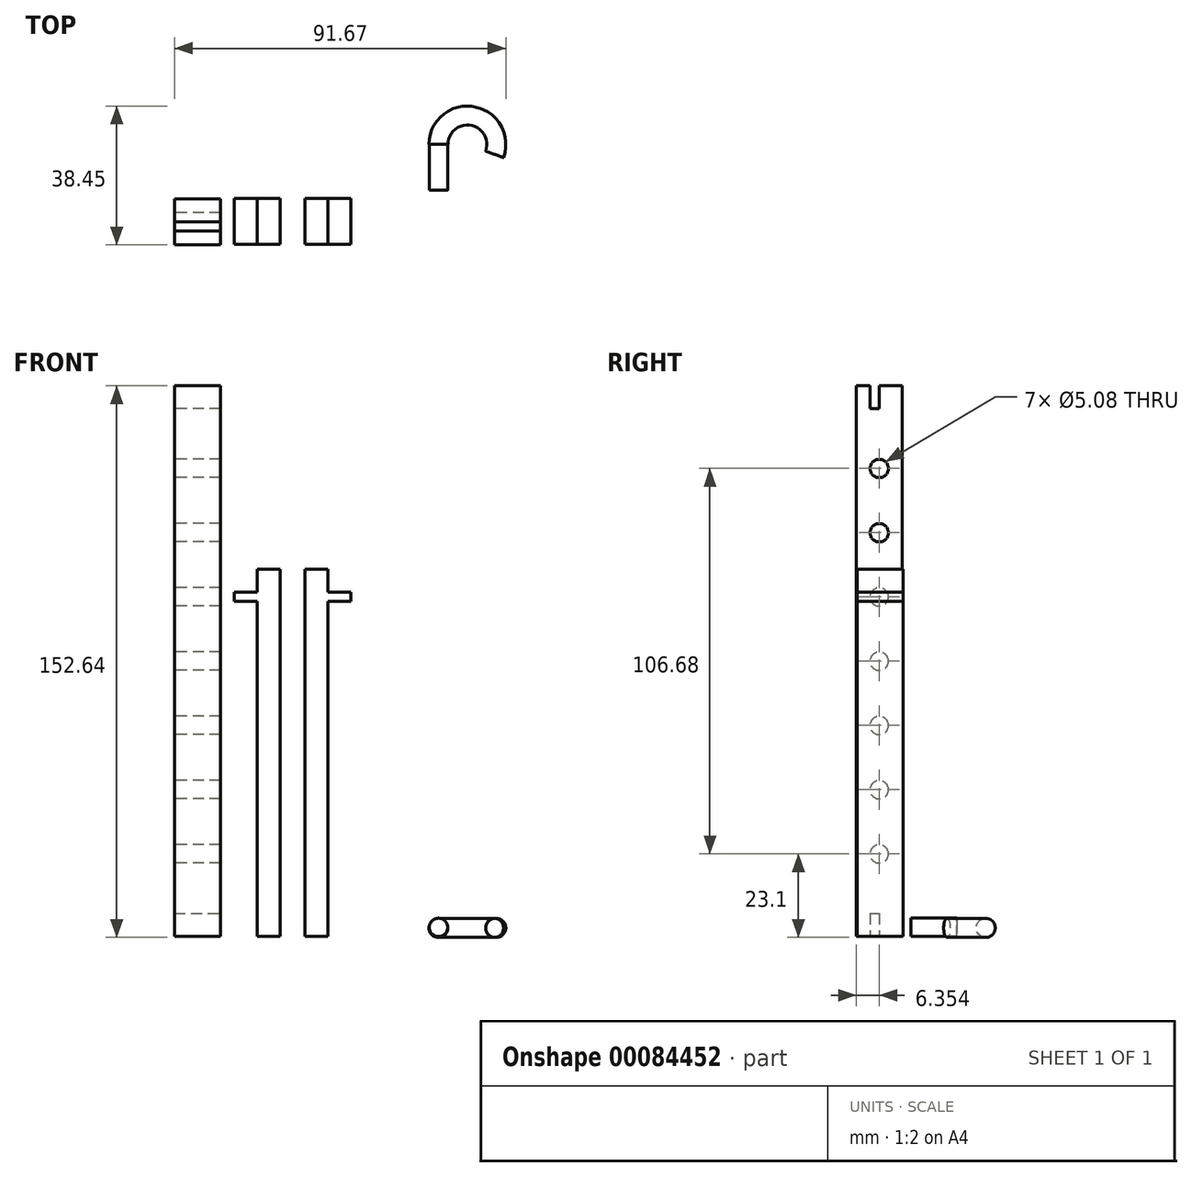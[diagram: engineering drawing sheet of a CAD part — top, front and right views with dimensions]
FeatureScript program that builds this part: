
annotation { "Feature Type Name" : "Feature", "Feature Type Description" : "" }
export const myFeature = defineFeature(function(context is Context, id is Id, definition is map)
    precondition{}
    {
        {
            var Q0;
            Q0=qCreatedBy(makeId("Top.planeOp"),FACE);
            var sketch = newSketch(context, id + "F0", { "sketchPlane" : qUnion([Q0])});
            skLineSegment(sketch, "E0.bottom", {"start": v(-10.38, -28.84) * mm, "end": v(-4.03, -28.84) * mm});
            skLineSegment(sketch, "E0.top", {"start": v(-10.38, -41.54) * mm, "end": v(-4.03, -41.54) * mm});
            skLineSegment(sketch, "E0.left", {"start": v(-10.38, -28.84) * mm, "end": v(-10.38, -41.54) * mm});
            skLineSegment(sketch, "E0.right", {"start": v(-4.03, -28.84) * mm, "end": v(-4.03, -41.54) * mm});
            skLineSegment(sketch, "E1.bottom", {"start": v(2.83, -28.77) * mm, "end": v(9.18, -28.77) * mm});
            skLineSegment(sketch, "E1.top", {"start": v(2.83, -41.47) * mm, "end": v(9.18, -41.47) * mm});
            skLineSegment(sketch, "E1.left", {"start": v(2.83, -28.77) * mm, "end": v(2.83, -41.47) * mm});
            skLineSegment(sketch, "E1.right", {"start": v(9.18, -28.77) * mm, "end": v(9.18, -41.47) * mm});
            skSolve(sketch);
        }
        {
            var Q0;
            Q0 = qSketchRegion(id + "F0", true);
            extrude(context, id + "F1", {"entities" : qUnion([Q0]), "depth" : 101.6 * mm});
        }
        {
            var Q0;
            Q0=makeQuery(id+"F1.opExtrude","SWEPT_FACE",FACE,{"disambiguationData":[OSD([sQuery(id+"F0.wireOp",EDGE,"E1.right")])]});
            var sketch = newSketch(context, id + "F2", { "sketchPlane" : qUnion([Q0])});
            skLineSegment(sketch, "E2.bottom", {"start": v(-41.47, 95.25) * mm, "end": v(-28.77, 95.25) * mm});
            skLineSegment(sketch, "E2.top", {"start": v(-41.47, 92.71) * mm, "end": v(-28.77, 92.71) * mm});
            skLineSegment(sketch, "E2.left", {"start": v(-41.47, 95.25) * mm, "end": v(-41.47, 92.71) * mm});
            skLineSegment(sketch, "E2.right", {"start": v(-28.77, 95.25) * mm, "end": v(-28.77, 92.71) * mm});
            skSolve(sketch);
        }
        {
            var Q0;
            Q0 = qSketchRegion(id + "F2", true);
            extrude(context, id + "F3", {"entities" : qUnion([Q0]), "operationType" : NewBodyOperationType.ADD, "depth" : 6.35 * mm});
        }
        {
            var Q0;
            Q0=makeQuery(id+"F1.opExtrude","SWEPT_FACE",FACE,{"disambiguationData":[OSD([sQuery(id+"F0.wireOp",EDGE,"E0.left")])]});
            var sketch = newSketch(context, id + "F4", { "sketchPlane" : qUnion([Q0])});
            skLineSegment(sketch, "E3.bottom", {"start": v(28.84, 95.25) * mm, "end": v(41.54, 95.25) * mm});
            skLineSegment(sketch, "E3.top", {"start": v(28.84, 92.71) * mm, "end": v(41.54, 92.71) * mm});
            skLineSegment(sketch, "E3.left", {"start": v(28.84, 95.25) * mm, "end": v(28.84, 92.71) * mm});
            skLineSegment(sketch, "E3.right", {"start": v(41.54, 95.25) * mm, "end": v(41.54, 92.71) * mm});
            skSolve(sketch);
        }
        {
            var Q0;
            Q0 = qSketchRegion(id + "F4", true);
            extrude(context, id + "F5", {"entities" : qUnion([Q0]), "operationType" : NewBodyOperationType.ADD, "depth" : 6.35 * mm});
        }
        {
            var Q0;
            Q0=qCreatedBy(makeId("Top.planeOp"),FACE);
            var sketch = newSketch(context, id + "F6", { "sketchPlane" : qUnion([Q0])});
            skLineSegment(sketch, "E4.bottom", {"start": v(-20.6, -41.66) * mm, "end": v(-33.3, -41.66) * mm});
            skLineSegment(sketch, "E4.top", {"start": v(-20.6, -28.96) * mm, "end": v(-33.3, -28.96) * mm});
            skLineSegment(sketch, "E4.left", {"start": v(-20.6, -41.66) * mm, "end": v(-20.6, -28.96) * mm});
            skLineSegment(sketch, "E4.right", {"start": v(-33.3, -41.66) * mm, "end": v(-33.3, -28.96) * mm});
            skSolve(sketch);
        }
        {
            var Q0;
            Q0 = qSketchRegion(id + "F6", true);
            extrude(context, id + "F7", {"entities" : qUnion([Q0]), "depth" : 152.4 * mm});
        }
        {
            var Q0;
            Q0=makeQuery(id+"F7.opExtrude","CAP_FACE",FACE,{"disambiguationData":[OSD([sQuery(id+"F6.wireOp",EDGE,"E4.bottom"),sQuery(id+"F6.wireOp",EDGE,"E4.top"),sQuery(id+"F6.wireOp",EDGE,"E4.left"),sQuery(id+"F6.wireOp",EDGE,"E4.right")])],"isStart":false});
            var sketch = newSketch(context, id + "F8", { "sketchPlane" : qUnion([Q0])});
            skLineSegment(sketch, "E5.bottom", {"start": v(-20.6, -35.3) * mm, "end": v(-33.3, -35.3) * mm});
            skLineSegment(sketch, "E5.top", {"start": v(-20.6, -37.85) * mm, "end": v(-33.3, -37.85) * mm});
            skLineSegment(sketch, "E5.left", {"start": v(-20.6, -35.3) * mm, "end": v(-20.6, -37.85) * mm});
            skLineSegment(sketch, "E5.right", {"start": v(-33.3, -35.3) * mm, "end": v(-33.3, -37.85) * mm});
            skSolve(sketch);
        }
        {
            var Q0;
            Q0 = qSketchRegion(id + "F8", true);
            extrude(context, id + "F9", {"entities" : qUnion([Q0]), "operationType" : NewBodyOperationType.REMOVE, "oppositeDirection" : true, "depth" : 6.35 * mm});
        }
        {
            var Q0;
            Q0=makeQuery(id+"F7.opExtrude","CAP_FACE",FACE,{"disambiguationData":[OSD([sQuery(id+"F6.wireOp",EDGE,"E4.bottom"),sQuery(id+"F6.wireOp",EDGE,"E4.top"),sQuery(id+"F6.wireOp",EDGE,"E4.left"),sQuery(id+"F6.wireOp",EDGE,"E4.right")])],"isStart":true});
            var sketch = newSketch(context, id + "F10", { "sketchPlane" : qUnion([Q0])});
            skLineSegment(sketch, "E6.bottom", {"start": v(-33.3, 35.3) * mm, "end": v(-20.6, 35.3) * mm});
            skLineSegment(sketch, "E6.top", {"start": v(-33.3, 37.85) * mm, "end": v(-20.6, 37.85) * mm});
            skLineSegment(sketch, "E6.left", {"start": v(-33.3, 35.3) * mm, "end": v(-33.3, 37.85) * mm});
            skLineSegment(sketch, "E6.right", {"start": v(-20.6, 35.3) * mm, "end": v(-20.6, 37.85) * mm});
            skSolve(sketch);
        }
        {
            var Q0;
            Q0 = qSketchRegion(id + "F10", true);
            extrude(context, id + "F11", {"entities" : qUnion([Q0]), "operationType" : NewBodyOperationType.REMOVE, "oppositeDirection" : true, "depth" : 6.35 * mm});
        }
        {
            var Q0;
            Q0=makeQuery(id+"F7.opExtrude","SWEPT_FACE",FACE,{"disambiguationData":[OSD([sQuery(id+"F6.wireOp",EDGE,"E4.right")])]});
            var sketch = newSketch(context, id + "F12", { "sketchPlane" : qUnion([Q0])});
            skCircle(sketch, "E7", {"center": v(35.3, 22.86) * mm, "radius": 2.54 * mm});
            skCircle(sketch, "E8", {"center": v(35.3, 40.64) * mm, "radius": 2.54 * mm});
            skCircle(sketch, "E9", {"center": v(35.3, 76.2) * mm, "radius": 2.54 * mm});
            skCircle(sketch, "E10", {"center": v(35.3, 93.98) * mm, "radius": 2.54 * mm});
            skCircle(sketch, "E11", {"center": v(35.3, 111.76) * mm, "radius": 2.54 * mm});
            skCircle(sketch, "E12", {"center": v(35.3, 58.42) * mm, "radius": 2.54 * mm});
            skCircle(sketch, "E13", {"center": v(35.3, 129.54) * mm, "radius": 2.54 * mm});
            skSolve(sketch);
        }
        {
            var Q0;
            Q0 = qSketchRegion(id + "F12", true);
            extrude(context, id + "F13", {"entities" : qUnion([Q0]), "operationType" : NewBodyOperationType.REMOVE, "oppositeDirection" : true, "depth" : 12.7 * mm});
        }
        {
            var Q0;
            Q0=qCreatedBy(makeId("Top.planeOp"),FACE);
            var sketch = newSketch(context, id + "F14", { "sketchPlane" : qUnion([Q0])});
            skLineSegment(sketch, "E14.bottom", {"start": v(37.2, -13.85) * mm, "end": v(42.27, -13.85) * mm});
            skLineSegment(sketch, "E14.top", {"start": v(37.2, -26.55) * mm, "end": v(42.27, -26.55) * mm});
            skLineSegment(sketch, "E14.left", {"start": v(37.2, -13.85) * mm, "end": v(37.2, -26.55) * mm});
            skLineSegment(sketch, "E14.right", {"start": v(42.27, -13.85) * mm, "end": v(42.27, -26.55) * mm});
            skSolve(sketch);
        }
        {
            var Q0;
            Q0 = qSketchRegion(id + "F14", true);
            extrude(context, id + "F15", {"entities" : qUnion([Q0]), "depth" : 5.08 * mm});
        }
        {
            var Q0;
            Q0=makeQuery(id+"F15.opExtrude","CAP_EDGE",EDGE,{"disambiguationData":[OSD([sQuery(id+"F14.wireOp",EDGE,"E14.right")])],"isStart":false});
            var Q1;
            Q1=makeQuery(id+"F15.opExtrude","CAP_EDGE",EDGE,{"disambiguationData":[OSD([sQuery(id+"F14.wireOp",EDGE,"E14.left")])],"isStart":false});
            var Q2;
            Q2=makeQuery(id+"F15.opExtrude","CAP_EDGE",EDGE,{"disambiguationData":[OSD([sQuery(id+"F14.wireOp",EDGE,"E14.right")])],"isStart":true});
            var Q3;
            Q3=makeQuery(id+"F15.opExtrude","CAP_EDGE",EDGE,{"disambiguationData":[OSD([sQuery(id+"F14.wireOp",EDGE,"E14.left")])],"isStart":true});
            fillet(context, id + "F16", {"entities" : qUnion([Q0, Q1, Q2, Q3]), "radius" : 2.54 * mm, "tangentPropagation" : true, "allowEdgeOverflow" : false});
        }
        {
            var Q0;
            Q0=makeQuery(id+"F15.opExtrude","SWEPT_FACE",FACE,{"disambiguationData":[OSD([sQuery(id+"F14.wireOp",EDGE,"E14.bottom")])]});
            cPlane(context, id + "F17", {"entities" : qUnion([Q0]), "cplaneType" : CPlaneType.OFFSET, "offset" : 0 * mm, "width" : 152.4 * mm, "height" : 152.4 * mm});
        }
        {
            var Q0;
            Q0=qCreatedBy(id+"F17.planeOp",FACE);
            var sketch = newSketch(context, id + "F18", { "sketchPlane" : qUnion([Q0])});
            skCircle(sketch, "E15", {"center": v(-39.73, 2.4) * mm, "radius": 2.63 * mm});
            skLineSegment(sketch, "E16", {"start": v(-47.73, 13.36) * mm, "end": v(-47.73, -12.43) * mm});
            skSolve(sketch);
        }
        {
            var Q0;
            Q0=makeQuery(id+"F18.imprint","IMPRINT",FACE,{"disambiguationData":[TD([[makeQuery(id+"F18.imprint","IMPRINT",EDGE,{"derivedFrom":sQuery(id+"F18.wireOp",EDGE,"E15")}),1.0]])]});
            var Q1;
            Q1=sQuery(id+"F18.wireOp",EDGE,"E16");
            revolve(context, id + "F19", {"operationType" : NewBodyOperationType.ADD, "entities" : qUnion([Q0]), "axis" : qUnion([Q1]), "revolveType" : RevolveType.ONE_DIRECTION, "angle" : 200 * degree});
        }
    });
